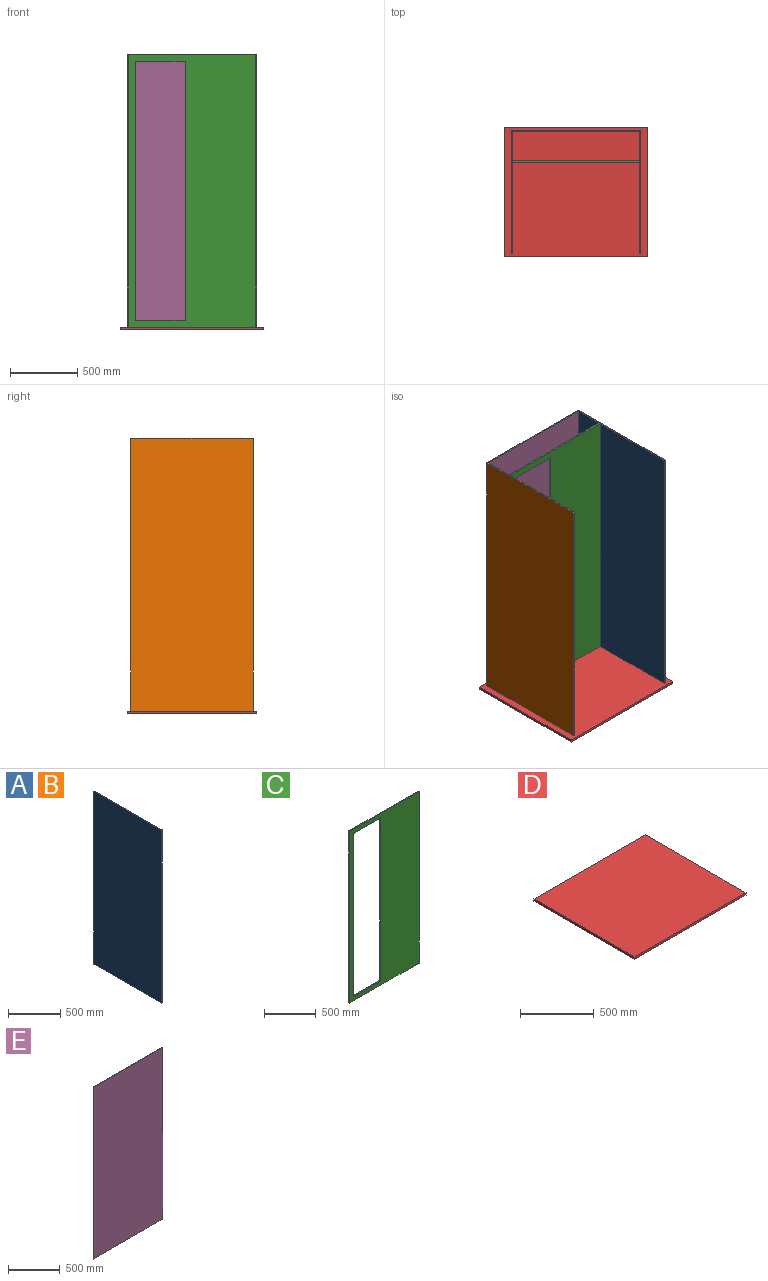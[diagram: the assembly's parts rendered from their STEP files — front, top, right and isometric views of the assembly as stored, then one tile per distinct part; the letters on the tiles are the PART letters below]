
ASSEMBLY  parts=5 mates=4
PART A: 6 faces, bbox 9.5x914.4x2032 mm
  f0: plane 914.4x9.53mm, normal (0,0,1), area 8709.7mm2, adj f1,f3,f4,f5
  f1: plane 2032x9.53mm, normal (0,-1,0), area 19354.8mm2, adj f0,f2,f4,f5
  f2: plane 914.4x9.53mm, normal (0,0,-1), area 8709.7mm2, adj f1,f3,f4,f5
  f3: plane 2032x9.53mm, normal (0,1,0), area 19354.8mm2, adj f0,f2,f4,f5
  f4: plane 2032x914.4mm, normal (1,0,0), area 1858060.8mm2, adj f0,f1,f2,f3
  f5: plane 2032x914.4mm, normal (-1,0,0), area 1858060.8mm2, adj f0,f1,f2,f3
PART B: same geometry as A
PART C: 10 faces, bbox 946.2x12.7x2032 mm
  f0: plane 2032x946.15mm, normal (0,-1,0), area 1205481.5mm2, adj f2,f3,f4,f5,f6,f7,f8,f9
  f1: plane 2032x946.15mm, normal (0,1,0), area 1205481.5mm2, adj f2,f3,f4,f5,f6,f7,f8,f9
  f2: plane 946.15x12.7mm, normal (0,0,1), area 12016.1mm2, adj f0,f1,f3,f5
  f3: plane 2032x12.7mm, normal (-1,0,0), area 25806.4mm2, adj f0,f1,f2,f4
  f4: plane 946.15x12.7mm, normal (0,0,-1), area 12016.1mm2, adj f0,f1,f3,f5
  f5: plane 2032x12.7mm, normal (1,0,0), area 25806.4mm2, adj f0,f1,f2,f4
  f6: plane 371.48x12.7mm, normal (0,0,-1), area 4717.7mm2, adj f0,f1,f7,f9
  f7: plane 1930.4x12.7mm, normal (1,0,0), area 24516.1mm2, adj f0,f1,f6,f8
  f8: plane 371.48x12.7mm, normal (0,0,1), area 4717.7mm2, adj f0,f1,f7,f9
  f9: plane 1930.4x12.7mm, normal (-1,0,0), area 24516.1mm2, adj f0,f1,f6,f8
PART D: 6 faces, bbox 1066.8x965.2x19.1 mm
  f0: plane 1066.8x19.05mm, normal (0,1,0), area 20322.5mm2, adj f1,f3,f4,f5
  f1: plane 965.2x19.05mm, normal (-1,0,0), area 18387.1mm2, adj f0,f2,f4,f5
  f2: plane 1066.8x19.05mm, normal (0,-1,0), area 20322.5mm2, adj f1,f3,f4,f5
  f3: plane 965.2x19.05mm, normal (1,0,0), area 18387.1mm2, adj f0,f2,f4,f5
  f4: plane 1066.8x965.2mm, normal (0,0,1), area 1029675.4mm2, adj f0,f1,f2,f3
  f5: plane 1066.8x965.2mm, normal (0,0,-1), area 1029675.4mm2, adj f0,f1,f2,f3
PART E: 6 faces, bbox 946.2x9.5x2032 mm
  f0: plane 946.15x9.53mm, normal (0,0,1), area 9012.1mm2, adj f1,f3,f4,f5
  f1: plane 2032x9.53mm, normal (-1,0,0), area 19354.8mm2, adj f0,f2,f4,f5
  f2: plane 946.15x9.53mm, normal (0,0,-1), area 9012.1mm2, adj f1,f3,f4,f5
  f3: plane 2032x9.53mm, normal (1,0,0), area 19354.8mm2, adj f0,f2,f4,f5
  f4: plane 2032x946.15mm, normal (0,-1,0), area 1922576.8mm2, adj f0,f1,f2,f3
  f5: plane 2032x946.15mm, normal (0,1,0), area 1922576.8mm2, adj f0,f1,f2,f3
PLACE A t=(473.08,0,19.05)mm
PLACE B t=(-482.6,0,19.05)mm
PLACE C t=(0,225.42,19.05)mm
PLACE D at identity
PLACE E t=(0,452.44,19.05)mm
MATE fastened B.f2 <-> D.f4  axis (0,0,-1) through (-477.84,0,19.05)mm
MATE fastened A.f2 <-> D.f4  axis (0,0,-1) through (477.84,0,19.05)mm
MATE fastened E.f2 <-> D.f4  axis (0,0,-1) through (0,452.44,19.05)mm
MATE fastened C.f4 <-> D.f4  axis (0,0,-1) through (0,225.42,19.05)mm
